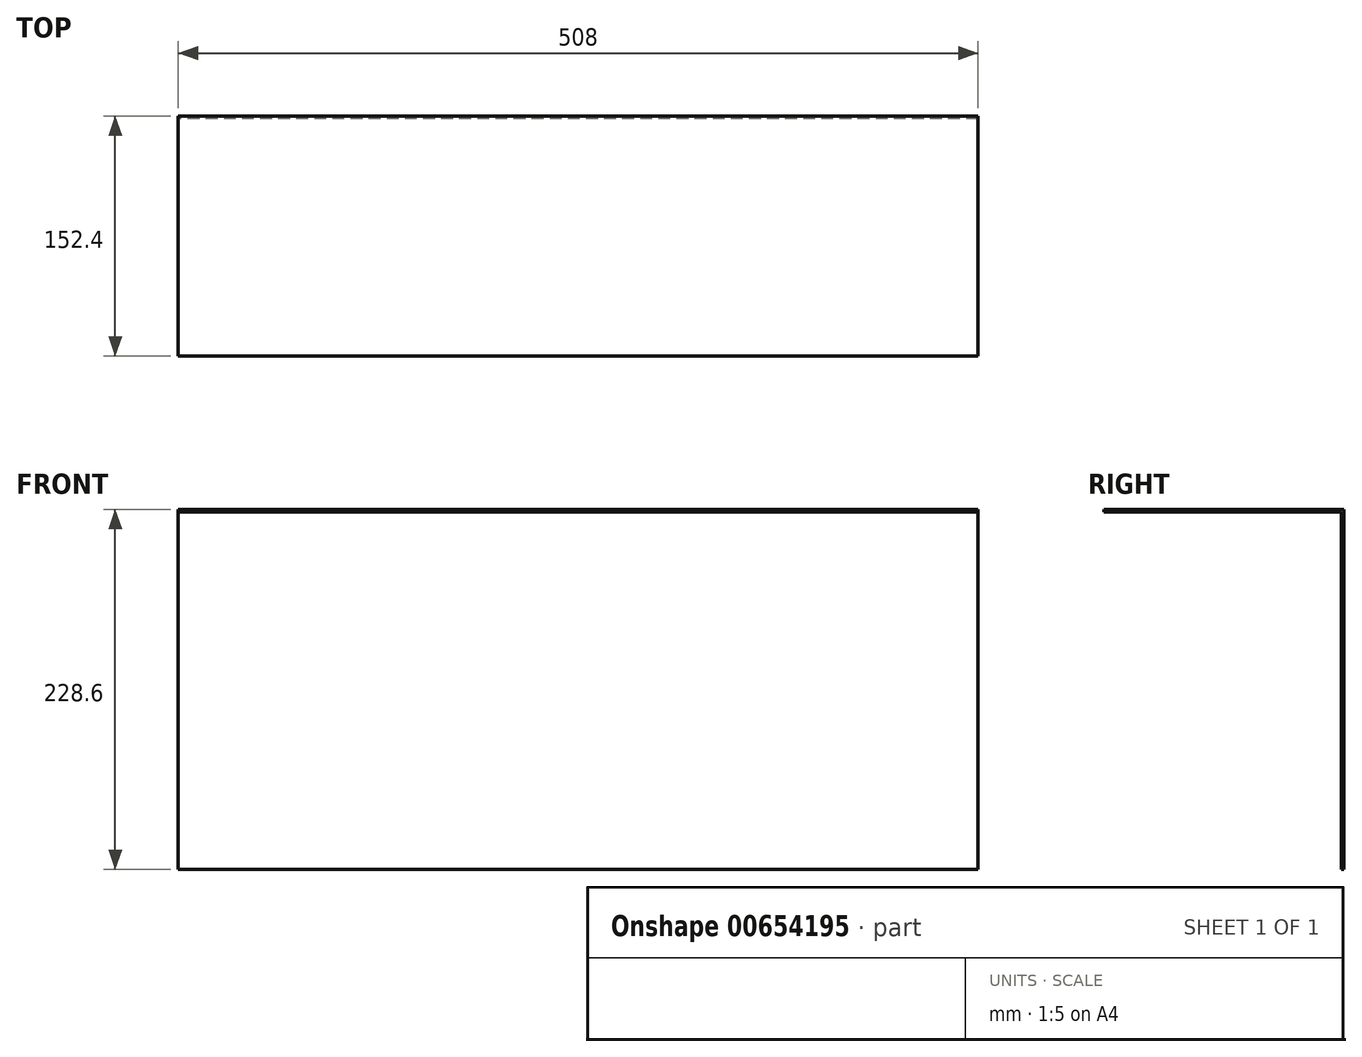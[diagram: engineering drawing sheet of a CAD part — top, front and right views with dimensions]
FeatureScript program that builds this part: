
annotation { "Feature Type Name" : "Feature", "Feature Type Description" : "" }
export const myFeature = defineFeature(function(context is Context, id is Id, definition is map)
    precondition{}
    {
        {
            var Q0;
            Q0=qCreatedBy(makeId("Right.planeOp"),FACE);
            var sketch = newSketch(context, id + "F0", { "sketchPlane" : qUnion([Q0])});
            skLineSegment(sketch, "E0", {"start": v(16.15, -1.18) * mm, "end": v(16.15, 0.4) * mm});
            skLineSegment(sketch, "E1", {"start": v(16.15, 0.4) * mm, "end": v(168.55, 0.4) * mm});
            skLineSegment(sketch, "E2", {"start": v(168.55, 0.4) * mm, "end": v(168.55, -228.2) * mm});
            skLineSegment(sketch, "E3", {"start": v(168.55, -228.2) * mm, "end": v(166.98, -228.2) * mm});
            skLineSegment(sketch, "E4", {"start": v(166.98, -228.2) * mm, "end": v(166.98, -1.18) * mm});
            skLineSegment(sketch, "E5", {"start": v(166.98, -1.18) * mm, "end": v(16.15, -1.18) * mm});
            skSolve(sketch);
        }
        {
            var Q0;
            Q0=makeQuery(id+"F0.imprint","IMPRINT",FACE,{"disambiguationData":[TD([[makeQuery(id+"F0.imprint","IMPRINT",EDGE,{"derivedFrom":sQuery(id+"F0.wireOp",EDGE,"E0")}),-1.0]])]});
            extrude(context, id + "F1", {"entities" : qUnion([Q0]), "depth" : 508 * mm, "offsetDistance" : 25.4 * mm});
        }
    });
